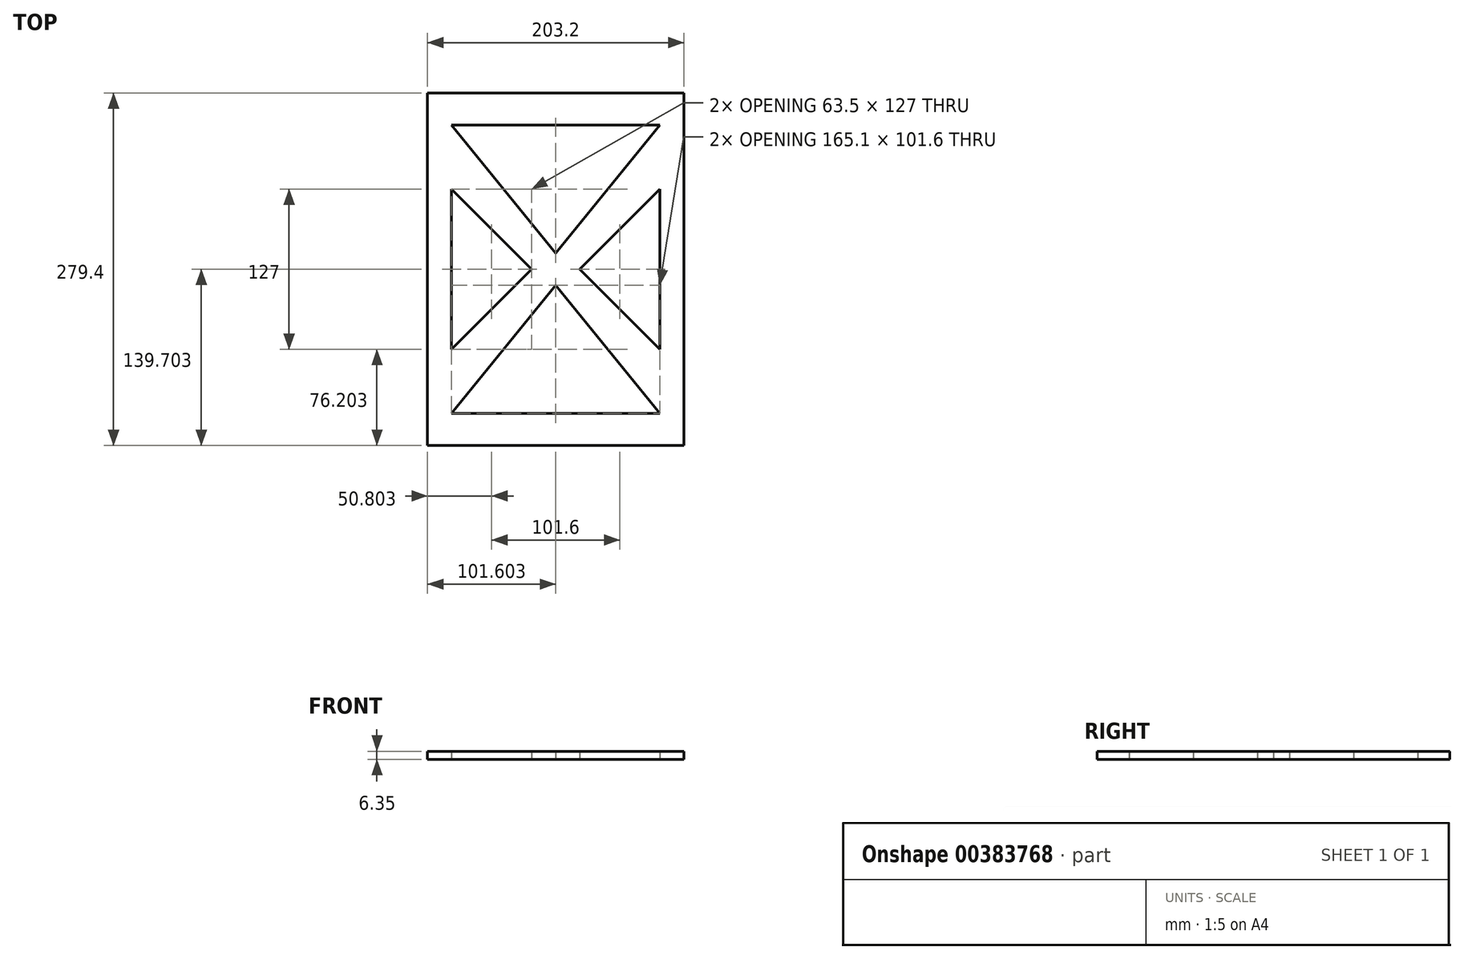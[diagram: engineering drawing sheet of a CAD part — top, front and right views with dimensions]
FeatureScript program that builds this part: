
annotation { "Feature Type Name" : "Feature", "Feature Type Description" : "" }
export const myFeature = defineFeature(function(context is Context, id is Id, definition is map)
    precondition{}
    {
        {
            var Q0;
            Q0=qCreatedBy(makeId("Top.planeOp"),FACE);
            var sketch = newSketch(context, id + "F0", { "sketchPlane" : qUnion([Q0])});
            skLineSegment(sketch, "E0.bottom", {"start": v(-62.77, -97.87) * mm, "end": v(140.43, -97.87) * mm});
            skLineSegment(sketch, "E0.top", {"start": v(-62.77, 181.53) * mm, "end": v(140.43, 181.53) * mm});
            skLineSegment(sketch, "E1.0", {"start": v(-43.72, 156.13) * mm, "end": v(121.38, 156.13) * mm});
            skLineSegment(sketch, "E2", {"start": v(38.83, 54.53) * mm, "end": v(121.38, 156.13) * mm});
            skLineSegment(sketch, "E3", {"start": v(38.83, 54.53) * mm, "end": v(-43.72, 156.13) * mm});
            skPoint(sketch, "E4.endSnap0", {"position": v(146.78, 41.83) * mm});
            skLineSegment(sketch, "E5.MirrorCS", {"start": v(38.83, 29.13) * mm, "end": v(121.38, -72.47) * mm});
            skLineSegment(sketch, "E6.MirrorCS", {"start": v(38.83, 29.13) * mm, "end": v(-43.72, -72.47) * mm});
            skLineSegment(sketch, "E7.MirrorCS", {"start": v(-43.72, -72.47) * mm, "end": v(121.38, -72.47) * mm});
            skLineSegment(sketch, "E8", {"start": v(-43.72, 105.33) * mm, "end": v(19.78, 41.83) * mm});
            skLineSegment(sketch, "E9", {"start": v(19.78, 41.83) * mm, "end": v(-43.72, -21.67) * mm});
            skLineSegment(sketch, "E10.trimOffspring", {"start": v(-43.72, -21.67) * mm, "end": v(-43.72, 105.33) * mm});
            skLineSegment(sketch, "E11.MirrorCS", {"start": v(57.88, 41.83) * mm, "end": v(121.38, -21.67) * mm});
            skLineSegment(sketch, "E12.MirrorCS", {"start": v(121.38, -21.67) * mm, "end": v(121.38, 105.33) * mm});
            skLineSegment(sketch, "E13.MirrorCS", {"start": v(121.38, 105.33) * mm, "end": v(57.88, 41.83) * mm});
            skLineSegment(sketch, "E14.0", {"start": v(-62.77, -97.87) * mm, "end": v(-62.77, 181.53) * mm});
            skLineSegment(sketch, "E15.0", {"start": v(140.43, -97.87) * mm, "end": v(140.43, 181.53) * mm});
            skSolve(sketch);
        }
        {
            var Q0;
            Q0=makeQuery(id+"F0.imprint","IMPRINT",FACE,{"disambiguationData":[TD([[makeQuery(id+"F0.imprint","IMPRINT",EDGE,{"derivedFrom":sQuery(id+"F0.wireOp",EDGE,"E0.bottom")}),1.0]])]});
            extrude(context, id + "F1", {"entities" : qUnion([Q0]), "depth" : 6.35 * mm});
        }
    });
